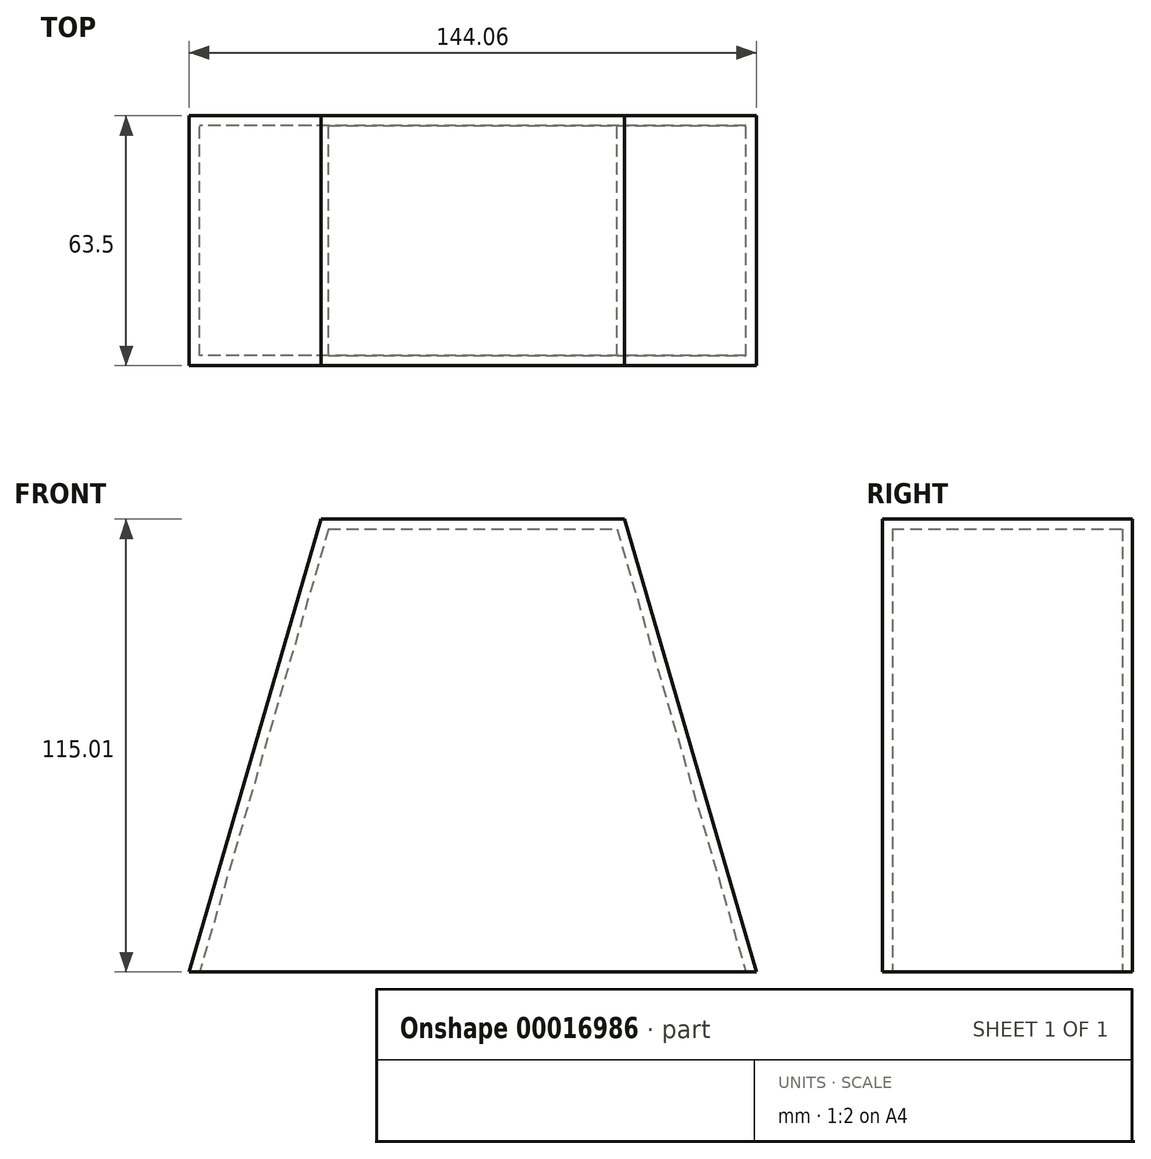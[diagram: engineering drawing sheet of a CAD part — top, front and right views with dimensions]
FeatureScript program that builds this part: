
annotation { "Feature Type Name" : "Feature", "Feature Type Description" : "" }
export const myFeature = defineFeature(function(context is Context, id is Id, definition is map)
    precondition{}
    {
        {
            var Q0;
            Q0=qCreatedBy(makeId("Front.planeOp"),FACE);
            var sketch = newSketch(context, id + "F0", { "sketchPlane" : qUnion([Q0])});
            skLineSegment(sketch, "E0", {"start": v(0, 106.97) * mm, "end": v(0, 0) * mm, "construction": true});
            skLineSegment(sketch, "E1", {"start": v(0, 75.94) * mm, "end": v(-12.3, 75.94) * mm, "construction": true});
            skLineSegment(sketch, "E2", {"start": v(-12.3, 75.94) * mm, "end": v(-12.3, 70.42) * mm, "construction": true});
            skLineSegment(sketch, "E3", {"start": v(0, 0) * mm, "end": v(-12.3, 0) * mm});
            skLineSegment(sketch, "E4", {"start": v(-12.3, 70.42) * mm, "end": v(-22.54, 70.42) * mm});
            skLineSegment(sketch, "E5", {"start": v(-22.54, 70.42) * mm, "end": v(-22.54, 4.76) * mm});
            skLineSegment(sketch, "E6", {"start": v(-22.54, 4.76) * mm, "end": v(-11.88, 4.76) * mm});
            skLineSegment(sketch, "E7", {"start": v(-11.88, 4.76) * mm, "end": v(-12.3, 0) * mm});
            skSolve(sketch);
        }
        {
            var Q0;
            Q0=qCreatedBy(makeId("Front.planeOp"),FACE);
            var sketch = newSketch(context, id + "F1", { "sketchPlane" : qUnion([Q0])});
            skLineSegment(sketch, "E8.0", {"start": v(-12.3, 75.94) * mm, "end": v(-12.3, 70.42) * mm});
            skLineSegment(sketch, "E9.0", {"start": v(0, 75.94) * mm, "end": v(-12.3, 75.94) * mm});
            skSolve(sketch);
        }
        {
            var Q0;
            Q0 = qSketchRegion(id + "F0", true);
            var Q1;
            Q1=sQuery(id+"F0.wireOp",EDGE,"E3");
            var Q2;
            Q2=sQuery(id+"F0.wireOp",EDGE,"E7");
            var Q3;
            Q3=sQuery(id+"F0.wireOp",EDGE,"E6");
            var Q4;
            Q4=sQuery(id+"F0.wireOp",EDGE,"E5");
            var Q5;
            Q5=sQuery(id+"F0.wireOp",EDGE,"E4");
            var Q6;
            Q6=sQuery(id+"F1.wireOp",EDGE,"E8.0");
            var Q7;
            Q7=sQuery(id+"F1.wireOp",EDGE,"E9.0");
            var Q8;
            Q8=sQuery(id+"F0.wireOp",EDGE,"E0");
            revolve(context, id + "F2", {"bodyType" : ToolBodyType.SURFACE, "entities" : qUnion([Q0]), "surfaceEntities" : qUnion([Q1, Q2, Q3, Q4, Q5, Q6, Q7]), "axis" : qUnion([Q8]), "revolveType" : RevolveType.FULL});
        }
        {
            var Q0;
            Q0=qCreatedBy(makeId("Front.planeOp"),FACE);
            var sketch = newSketch(context, id + "F3", { "sketchPlane" : qUnion([Q0])});
            skLineSegment(sketch, "E10", {"start": v(0, 5.16) * mm, "end": v(-38.55, 5.16) * mm});
            skLineSegment(sketch, "E11", {"start": v(-38.55, 5.16) * mm, "end": v(-72.03, -109.85) * mm});
            skLineSegment(sketch, "E12", {"start": v(0, -109.85) * mm, "end": v(-72.03, -109.85) * mm});
            skLineSegment(sketch, "E13", {"start": v(0, 5.16) * mm, "end": v(0, -109.85) * mm, "construction": true});
            skLineSegment(sketch, "E14.MirrorCS", {"start": v(0, 5.16) * mm, "end": v(38.55, 5.16) * mm});
            skLineSegment(sketch, "E15.MirrorCS", {"start": v(38.55, 5.16) * mm, "end": v(72.03, -109.85) * mm});
            skLineSegment(sketch, "E16.MirrorCS", {"start": v(0, -109.85) * mm, "end": v(72.03, -109.85) * mm});
            skLineSegment(sketch, "E17.MirrorCS", {"start": v(-38.55, 5.16) * mm, "end": v(-72.03, -109.85) * mm, "construction": true});
            skLineSegment(sketch, "E18.MirrorCS", {"start": v(0, -109.85) * mm, "end": v(-72.03, -109.85) * mm, "construction": true});
            skSolve(sketch);
        }
        {
            var Q0;
            Q0=makeQuery(id+"F3.imprint","IMPRINT",FACE,{"disambiguationData":[TD([[makeQuery(id+"F3.imprint","IMPRINT",EDGE,{"derivedFrom":sQuery(id+"F3.wireOp",EDGE,"E10")}),1.0]])]});
            var Q1;
            Q1=sQuery(id+"F3.wireOp",EDGE,"E15.MirrorCS");
            var Q2;
            Q2=sQuery(id+"F3.wireOp",EDGE,"E14.MirrorCS");
            var Q3;
            Q3=sQuery(id+"F3.wireOp",EDGE,"E16.MirrorCS");
            var Q4;
            Q4=sQuery(id+"F3.wireOp",EDGE,"E12");
            var Q5;
            Q5=sQuery(id+"F3.wireOp",EDGE,"E11");
            var Q6;
            Q6=sQuery(id+"F3.wireOp",EDGE,"E10");
            extrude(context, id + "F4", {"entities" : qUnion([Q0]), "surfaceEntities" : qUnion([Q1, Q2, Q3, Q4, Q5, Q6]), "endBound" : BoundingType.SYMMETRIC, "depth" : 63.5 * mm});
        }
        {
            var Q0;
            Q0=makeQuery(id+"F4.opExtrude","SWEPT_FACE",FACE,{"disambiguationData":[OSD([sQuery(id+"F3.wireOp",EDGE,"E12"),sQuery(id+"F3.wireOp",EDGE,"E16.MirrorCS")])]});
            var Q1;
            Q1=makeQuery(id+"F4.opExtrude","SWEPT_BODY",BODY,{"disambiguationData":[OSD([sQuery(id+"F3.wireOp",EDGE,"E10"),sQuery(id+"F3.wireOp",EDGE,"E12"),sQuery(id+"F3.wireOp",EDGE,"E14.MirrorCS"),sQuery(id+"F3.wireOp",EDGE,"E15.MirrorCS"),sQuery(id+"F3.wireOp",EDGE,"E16.MirrorCS"),sQuery(id+"F3.wireOp",EDGE,"E11")])]});
            shell(context, id + "F5", {"entities" : qUnion([Q0]), "parts" : qUnion([Q1]), "thickness" : 2.54 * mm});
        }
    });
